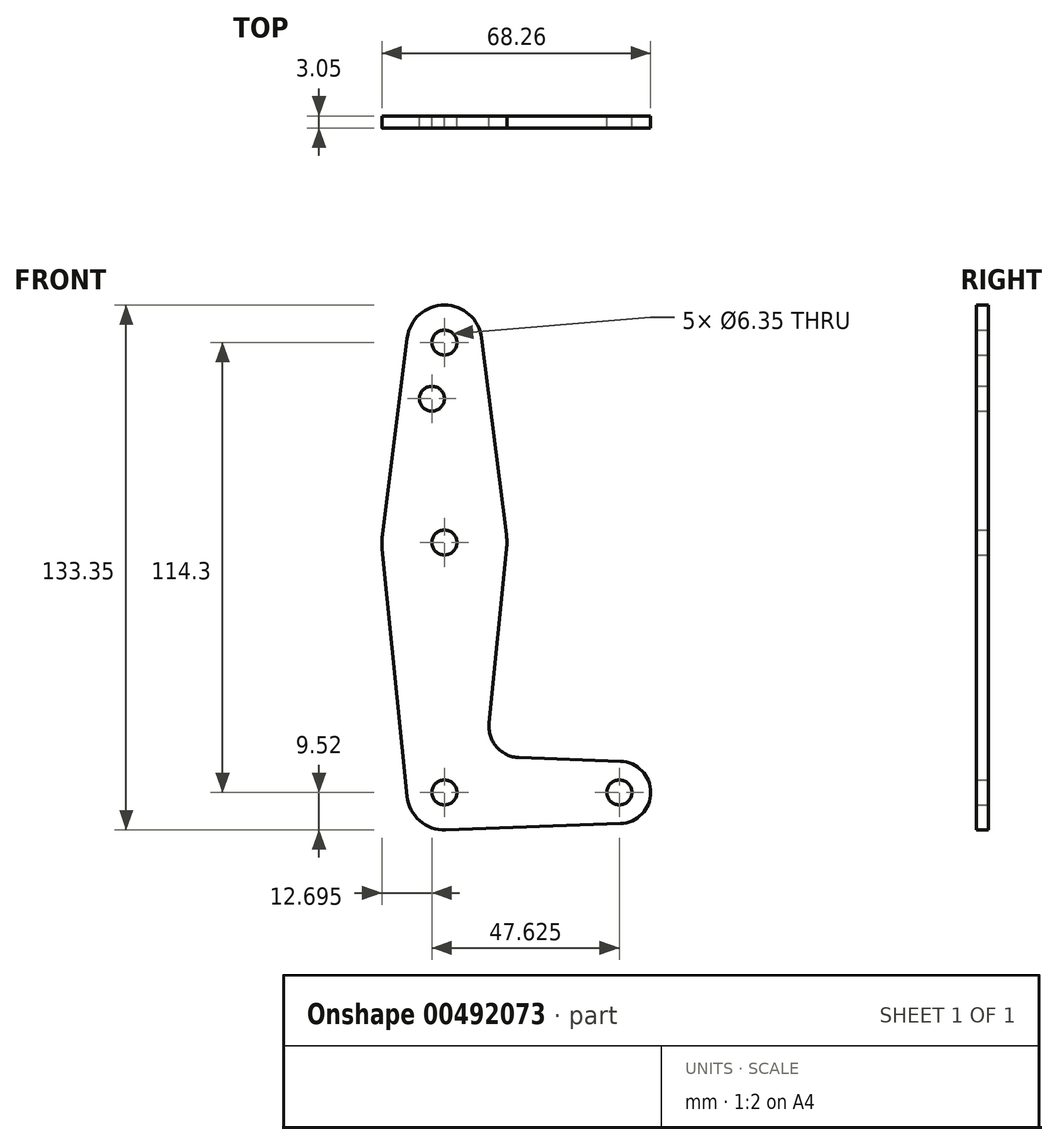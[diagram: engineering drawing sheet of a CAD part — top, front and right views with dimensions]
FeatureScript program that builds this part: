
annotation { "Feature Type Name" : "Feature", "Feature Type Description" : "" }
export const myFeature = defineFeature(function(context is Context, id is Id, definition is map)
    precondition{}
    {
        {
            var Q0;
            Q0=qCreatedBy(makeId("Front.planeOp"),FACE);
            var sketch = newSketch(context, id + "F0", { "sketchPlane" : qUnion([Q0])});
            skCircle(sketch, "E0", {"center": v(0, 0) * mm, "radius": 9.53 * mm});
            skCircle(sketch, "E1", {"center": v(0, 114.3) * mm, "radius": 9.53 * mm});
            skCircle(sketch, "E2", {"center": v(44.45, 0) * mm, "radius": 7.94 * mm});
            skCircle(sketch, "E3", {"center": v(0, 63.5) * mm, "radius": 15.88 * mm});
            skLineSegment(sketch, "E4", {"start": v(0, 114.3) * mm, "end": v(0, 0) * mm, "construction": true});
            skLineSegment(sketch, "E5", {"start": v(44.45, 0) * mm, "end": v(0, 0) * mm, "construction": true});
            skLineSegment(sketch, "E6", {"start": v(9.45, 115.5) * mm, "end": v(15.75, 65.48) * mm});
            skLineSegment(sketch, "E7", {"start": v(15.8, 61.91) * mm, "end": v(11.34, 17.6) * mm});
            skLineSegment(sketch, "E8", {"start": v(-15.75, 65.48) * mm, "end": v(-9.45, 115.5) * mm});
            skLineSegment(sketch, "E9", {"start": v(-15.8, 61.91) * mm, "end": v(-9.48, -0.95) * mm});
            skLineSegment(sketch, "E10", {"start": v(18.97, 8.85) * mm, "end": v(44.73, 7.93) * mm});
            skLineSegment(sketch, "E11", {"start": v(0.34, -9.52) * mm, "end": v(44.73, -7.93) * mm});
            skCircle(sketch, "E12", {"center": v(0, 114.3) * mm, "radius": 3.18 * mm});
            skCircle(sketch, "E13", {"center": v(-3.17, 100.03) * mm, "radius": 3.18 * mm});
            skCircle(sketch, "E14", {"center": v(0, 63.5) * mm, "radius": 3.18 * mm});
            skCircle(sketch, "E15", {"center": v(44.45, 0) * mm, "radius": 3.18 * mm});
            skCircle(sketch, "E16", {"center": v(0, 0) * mm, "radius": 3.18 * mm});
            skArc(sketch, "E17.filletArc", {"start": v(11.34, 17.6) * mm, "mid": v(13.26, 11.57) * mm, "end": v(18.97, 8.85) * mm});
            skSolve(sketch);
        }
        {
            var Q0;
            Q0 = qSketchRegion(id + "F0", true);
            extrude(context, id + "F1", {"entities" : qUnion([Q0]), "depth" : 3.05 * mm, "offsetDistance" : 25.4 * mm});
        }
    });
